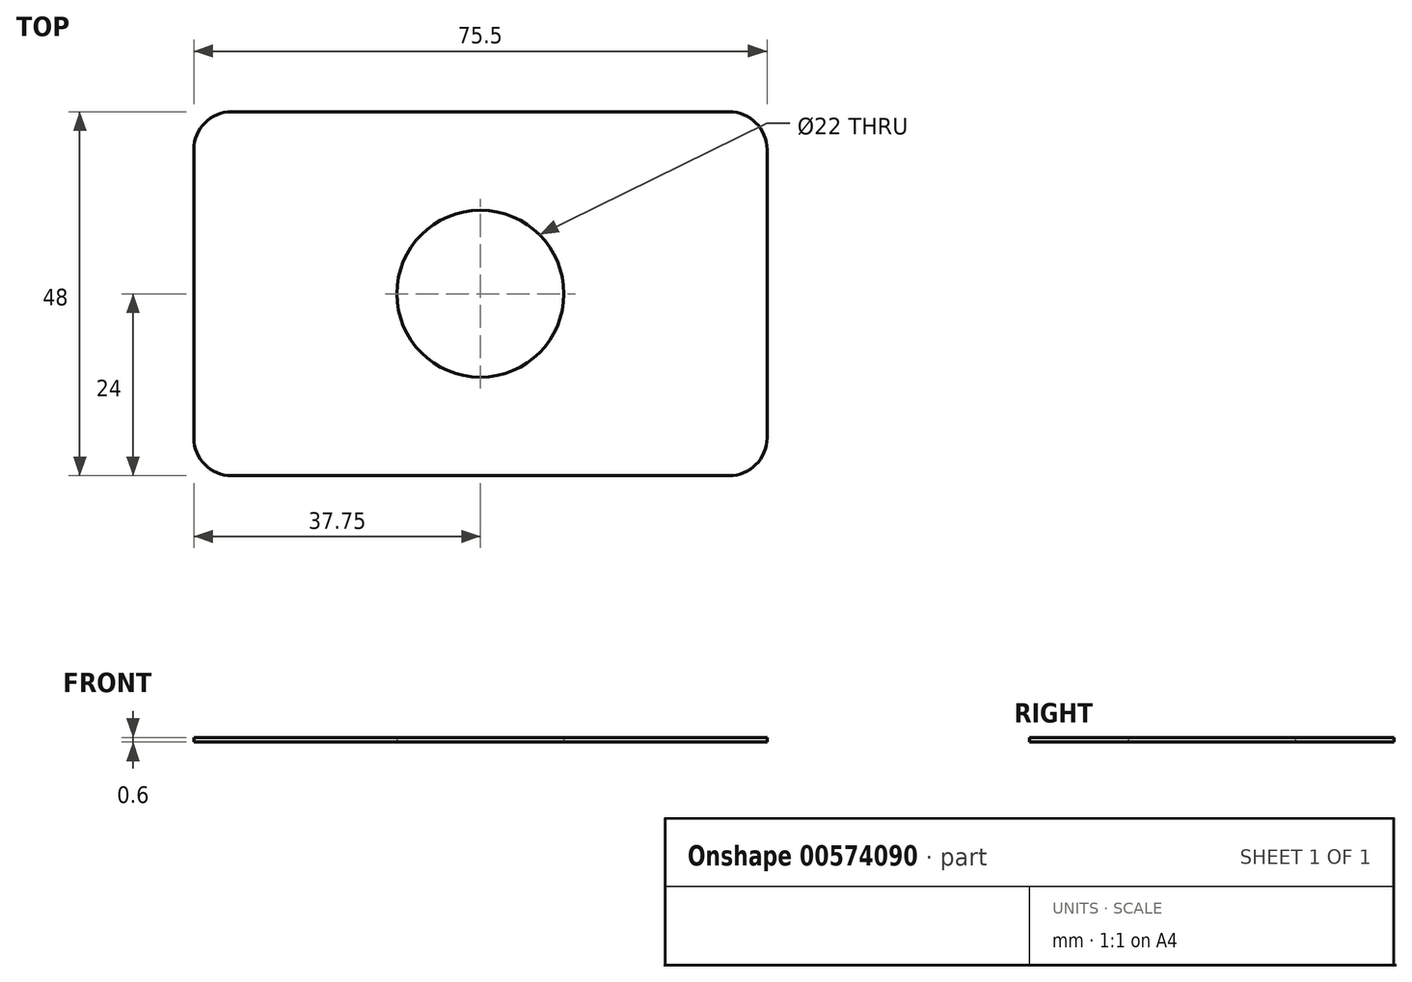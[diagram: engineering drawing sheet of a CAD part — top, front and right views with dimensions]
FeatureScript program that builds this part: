
annotation { "Feature Type Name" : "Feature", "Feature Type Description" : "" }
export const myFeature = defineFeature(function(context is Context, id is Id, definition is map)
    precondition{}
    {
        {
            var Q0;
            Q0=qCreatedBy(makeId("Top.planeOp"),FACE);
            var sketch = newSketch(context, id + "F0", { "sketchPlane" : qUnion([Q0])});
            skLineSegment(sketch, "E0.bottom", {"start": v(-32.75, 24) * mm, "end": v(32.75, 24) * mm});
            skLineSegment(sketch, "E0.top", {"start": v(-32.75, -24) * mm, "end": v(32.75, -24) * mm});
            skLineSegment(sketch, "E0.left", {"start": v(-37.75, 19) * mm, "end": v(-37.75, -19) * mm});
            skLineSegment(sketch, "E0.right", {"start": v(37.75, 19) * mm, "end": v(37.75, -19) * mm});
            skCircle(sketch, "E1", {"center": v(0, 0) * mm, "radius": 11 * mm});
            skPoint(sketch, "E2.visualSharp", {"position": v(-37.75, 24) * mm});
            skArc(sketch, "E2.filletArc", {"start": v(-32.75, 24) * mm, "mid": v(-36.29, 22.54) * mm, "end": v(-37.75, 19) * mm});
            skPoint(sketch, "E3.visualSharp", {"position": v(37.75, 24) * mm});
            skArc(sketch, "E3.filletArc", {"start": v(37.75, 19) * mm, "mid": v(36.29, 22.54) * mm, "end": v(32.75, 24) * mm});
            skPoint(sketch, "E4.visualSharp", {"position": v(37.75, -24) * mm});
            skArc(sketch, "E4.filletArc", {"start": v(32.75, -24) * mm, "mid": v(36.29, -22.54) * mm, "end": v(37.75, -19) * mm});
            skPoint(sketch, "E5.visualSharp", {"position": v(-37.75, -24) * mm});
            skArc(sketch, "E5.filletArc", {"start": v(-37.75, -19) * mm, "mid": v(-36.29, -22.54) * mm, "end": v(-32.75, -24) * mm});
            skSolve(sketch);
        }
        {
            var Q0;
            Q0 = qSketchRegion(id + "F0", true);
            extrude(context, id + "F1", {"entities" : qUnion([Q0]), "depth" : 0.6 * mm, "offsetDistance" : 25 * mm});
        }
    });
